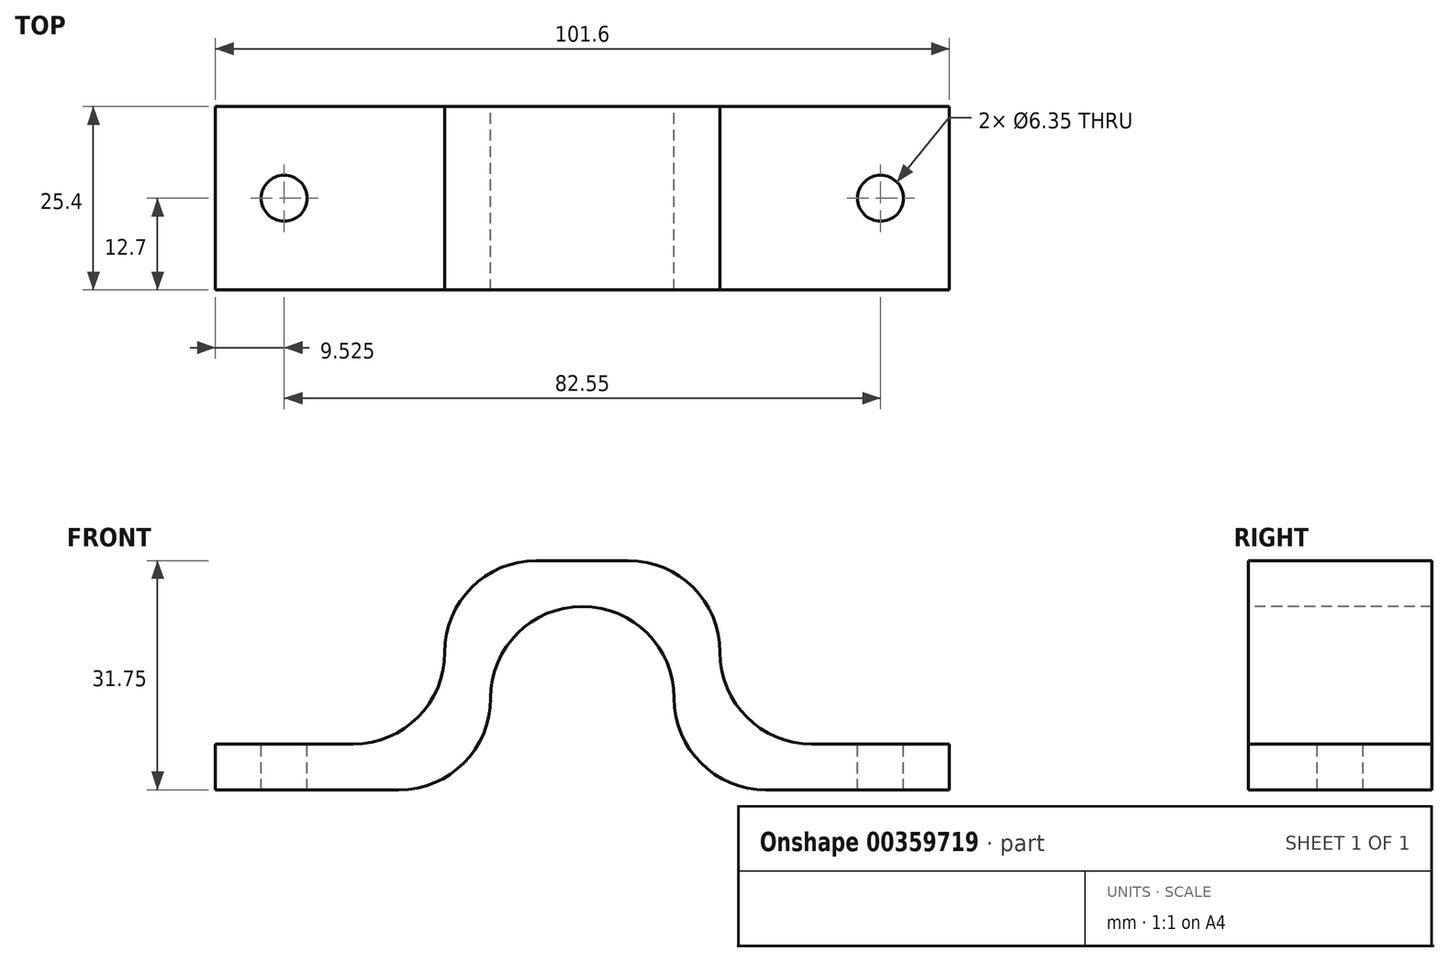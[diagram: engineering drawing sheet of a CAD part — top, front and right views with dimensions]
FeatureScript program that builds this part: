
annotation { "Feature Type Name" : "Feature", "Feature Type Description" : "" }
export const myFeature = defineFeature(function(context is Context, id is Id, definition is map)
    precondition{}
    {
        {
            var Q0;
            Q0=qCreatedBy(makeId("Front.planeOp"),FACE);
            var sketch = newSketch(context, id + "F0", { "sketchPlane" : qUnion([Q0])});
            skLineSegment(sketch, "E0", {"start": v(0, 0) * mm, "end": v(31.75, 0) * mm});
            skLineSegment(sketch, "E1", {"start": v(31.75, 0) * mm, "end": v(31.75, 25.4) * mm});
            skLineSegment(sketch, "E2", {"start": v(31.75, 25.4) * mm, "end": v(69.85, 25.4) * mm});
            skLineSegment(sketch, "E3", {"start": v(69.85, 25.4) * mm, "end": v(69.85, 0) * mm});
            skLineSegment(sketch, "E4", {"start": v(69.85, 0) * mm, "end": v(101.6, 0) * mm});
            skLineSegment(sketch, "E5.0", {"start": v(63.5, -6.35) * mm, "end": v(101.6, -6.35) * mm});
            skLineSegment(sketch, "E5.1", {"start": v(0, -6.35) * mm, "end": v(38.1, -6.35) * mm});
            skLineSegment(sketch, "E5.2", {"start": v(38.1, -6.35) * mm, "end": v(38.1, 19.05) * mm});
            skLineSegment(sketch, "E5.3", {"start": v(38.1, 19.05) * mm, "end": v(63.5, 19.05) * mm});
            skLineSegment(sketch, "E5.4", {"start": v(63.5, 19.05) * mm, "end": v(63.5, -6.35) * mm});
            skLineSegment(sketch, "E6", {"start": v(0, -6.35) * mm, "end": v(0, 0) * mm});
            skLineSegment(sketch, "E7", {"start": v(101.6, -6.35) * mm, "end": v(101.6, 0) * mm});
            skSolve(sketch);
        }
        {
            var Q0;
            Q0 = qSketchRegion(id + "F0", true);
            extrude(context, id + "F1", {"entities" : qUnion([Q0]), "depth" : 25.4 * mm});
        }
        {
            var Q0;
            Q0=makeQuery(id+"F1.opExtrude","SWEPT_EDGE",EDGE,{"disambiguationData":[OSD([sQuery(id+"F0.wireOp",EDGE,"E1"),sQuery(id+"F0.wireOp",EDGE,"E2")])]});
            var Q1;
            Q1=makeQuery(id+"F1.opExtrude","SWEPT_EDGE",EDGE,{"disambiguationData":[OSD([sQuery(id+"F0.wireOp",EDGE,"E5.2"),sQuery(id+"F0.wireOp",EDGE,"E5.3")])]});
            var Q2;
            Q2=makeQuery(id+"F1.opExtrude","SWEPT_EDGE",EDGE,{"disambiguationData":[OSD([sQuery(id+"F0.wireOp",EDGE,"E2"),sQuery(id+"F0.wireOp",EDGE,"E3")])]});
            var Q3;
            Q3=makeQuery(id+"F1.opExtrude","SWEPT_EDGE",EDGE,{"disambiguationData":[OSD([sQuery(id+"F0.wireOp",EDGE,"E5.3"),sQuery(id+"F0.wireOp",EDGE,"E5.4")])]});
            var Q4;
            Q4=makeQuery(id+"F1.opExtrude","SWEPT_EDGE",EDGE,{"disambiguationData":[OSD([sQuery(id+"F0.wireOp",EDGE,"E5.0"),sQuery(id+"F0.wireOp",EDGE,"E5.4")])]});
            var Q5;
            Q5=makeQuery(id+"F1.opExtrude","SWEPT_EDGE",EDGE,{"disambiguationData":[OSD([sQuery(id+"F0.wireOp",EDGE,"E3"),sQuery(id+"F0.wireOp",EDGE,"E4")])]});
            var Q6;
            Q6=makeQuery(id+"F1.opExtrude","SWEPT_EDGE",EDGE,{"disambiguationData":[OSD([sQuery(id+"F0.wireOp",EDGE,"E5.1"),sQuery(id+"F0.wireOp",EDGE,"E5.2")])]});
            var Q7;
            Q7=makeQuery(id+"F1.opExtrude","SWEPT_EDGE",EDGE,{"disambiguationData":[OSD([sQuery(id+"F0.wireOp",EDGE,"E0"),sQuery(id+"F0.wireOp",EDGE,"E1")])]});
            fillet(context, id + "F2", {"entities" : qUnion([Q0, Q1, Q2, Q3, Q4, Q5, Q6, Q7]), "radius" : 12.7 * mm, "tangentPropagation" : true, "allowEdgeOverflow" : false});
        }
        {
            var Q0;
            Q0=makeQuery(id+"F1.opExtrude","SWEPT_FACE",FACE,{"disambiguationData":[OSD([sQuery(id+"F0.wireOp",EDGE,"E0")])]});
            var sketch = newSketch(context, id + "F3", { "sketchPlane" : qUnion([Q0])});
            skCircle(sketch, "E8", {"center": v(9.53, -12.7) * mm, "radius": 3.18 * mm});
            skCircle(sketch, "E9", {"center": v(92.07, -12.7) * mm, "radius": 3.18 * mm});
            skSolve(sketch);
        }
        {
            var Q0;
            Q0=makeQuery(id+"F3.imprint","IMPRINT",FACE,{"disambiguationData":[TD([[makeQuery(id+"F3.imprint","IMPRINT",EDGE,{"derivedFrom":sQuery(id+"F3.wireOp",EDGE,"E8")}),1.0]])]});
            var Q1;
            Q1=makeQuery(id+"F3.imprint","IMPRINT",FACE,{"disambiguationData":[TD([[makeQuery(id+"F3.imprint","IMPRINT",EDGE,{"derivedFrom":sQuery(id+"F3.wireOp",EDGE,"E9")}),1.0]])]});
            extrude(context, id + "F4", {"entities" : qUnion([Q0, Q1]), "operationType" : NewBodyOperationType.REMOVE, "endBound" : BoundingType.THROUGH_ALL, "oppositeDirection" : true, "depth" : 25.4 * mm});
        }
    });
